# Revit family: BKEF-RH
name_source: partatom
category: Mechanical Equipment
units: mm (PartAtom-declared; Revit-internal decimal feet)

## family parameters
Always vertical = Yes
Cut with Voids When Loaded = No
OmniClass Number = 23.75.00.00
OmniClass Title = Climate Control (HVAC)
Part Type = Breaks Into
Room Calculation Point = No
Round Connector Dimension = Use Diameter
Shared = No
Work Plane-Based = No

## types (4) — shared parameters
A = 500 mm  [stored 1.64042 ft]
C = 420 mm  [stored 1.37795 ft]
D = 350 mm  [stored 1.14829 ft]
Description = Duct Fan
Frequency = 50 Hz
Insulation Class = F
Manufacturer = Bahçıvan Elektrik Motor San. ve Tic. Ltd. Şti.
Material = <By Category>
Model = BKEF-RH
Protection Class = 55
R = 150 mm
RD = 167 mm
URL = http://www.bahcivanmotor.com.tr

## per-type parameters (varying)
| type | Air Flow | B | Capacitor | Current | Power | Sound Pressure Level dB(A) | Speed ( d/d ) | Voltage | Weight |
| BKEF-RH 280M | 3600.0 m³/h | 500 mm  [stored 1.64042 ft] | 30 | 5 A | 750 W | 65 | 2840 | 230 V | 38.00 kg |
| BKEF-RH 315M | 5000.0 m³/h | 540 mm  [stored 1.77165 ft] | 40 | 10 A | 1500 W | 68 | 2865 | 230 V | 41.00 kg |
| BKEF-RH 280T | 3600.0 m³/h | 500 mm  [stored 1.64042 ft] | 0 | 2 A | 750 W | 65 | 2840 | 380 V | 38.00 kg |
| BKEF-RH 315T | 5000.0 m³/h | 540 mm  [stored 1.77165 ft] | 0 | 3 A | 1500 W | 68 | 2865 | 380 V | 41.00 kg |

note: [stored X ft] marks values corroborated as IEEE doubles in the binary element streams (Revit-internal decimal feet)

## geometry (parser evidence)
native form markers: Sweep x2
no freeform markers — native parametric forms only
